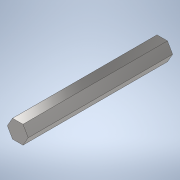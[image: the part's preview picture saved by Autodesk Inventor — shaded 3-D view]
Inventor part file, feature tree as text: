
AUTODESK INVENTOR PART (.ipt)
format: ipt  version: 2020 (Build 240168000, 168)  size: 99,840 bytes
history: native  units: in
note: dims shown in document units (in); Inventor stores cm internally (conversion verified against a paired STEP export)
features: extrude x1, sketch x1
ambient origin geometry x8: Origin, YZ Plane, XZ Plane, XY Plane, X Axis, Y Axis, Z Axis, Center Point
bodies: Solid1 (feature_tree)
feature tree (2):
  extrude  "Extrusion1"  Depth=4.0in TaperAngle=0.0deg
  sketch  "Sketch1"  dims[d0=0.5in d1=4.0in d2=0.0in]
